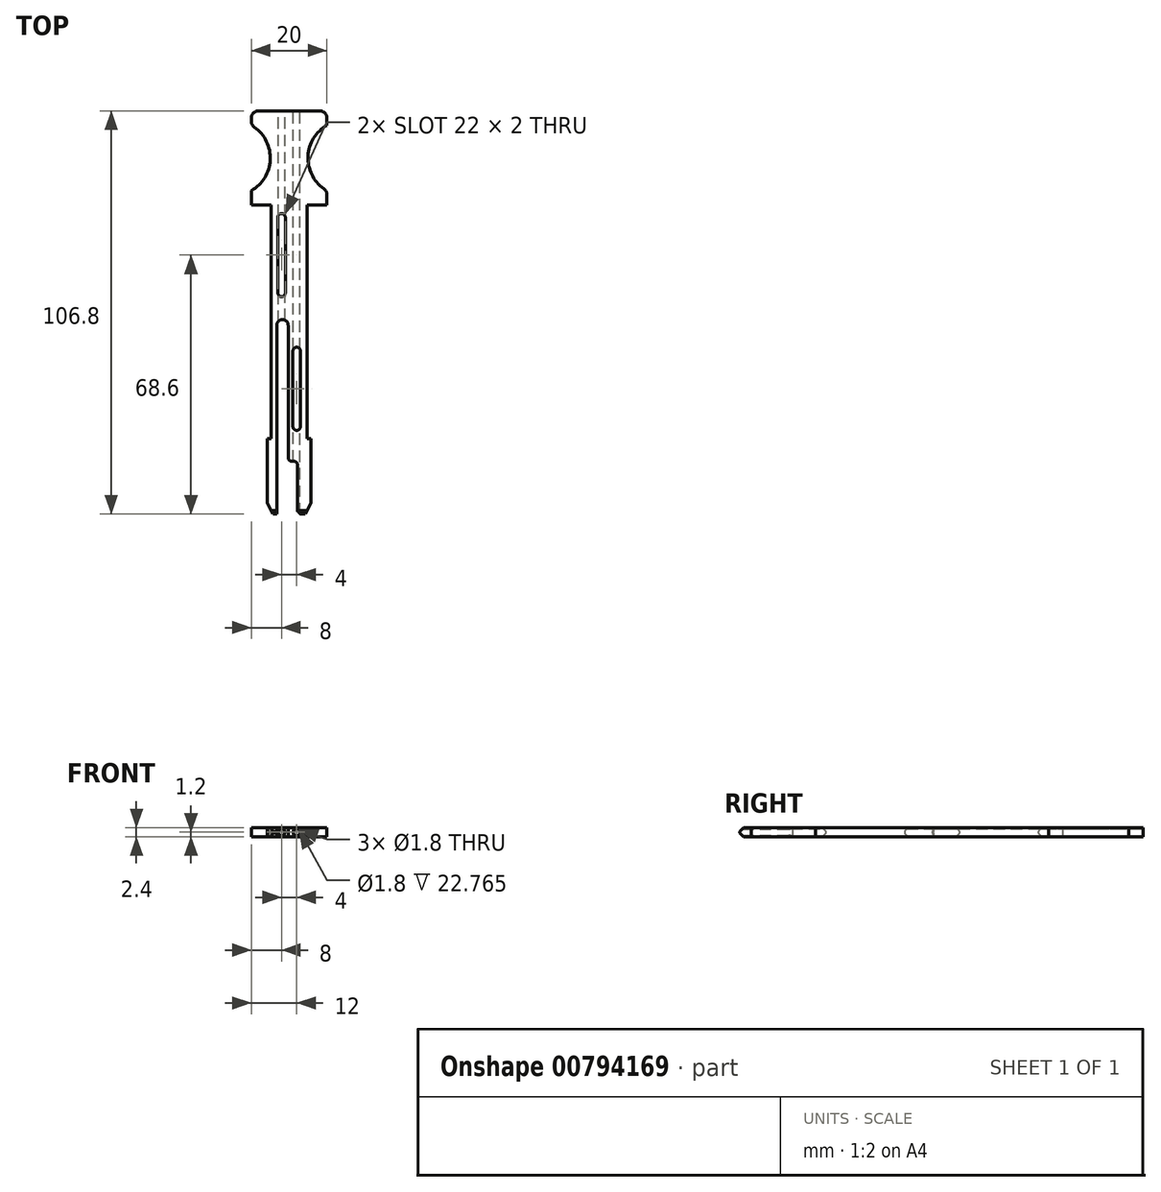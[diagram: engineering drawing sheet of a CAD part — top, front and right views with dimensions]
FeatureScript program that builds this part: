
annotation { "Feature Type Name" : "Feature", "Feature Type Description" : "" }
export const myFeature = defineFeature(function(context is Context, id is Id, definition is map)
    precondition{}
    {
        {
            var Q0;
            Q0=qCreatedBy(makeId("Top.planeOp"),FACE);
            var sketch = newSketch(context, id + "F0", { "sketchPlane" : qUnion([Q0])});
            skLineSegment(sketch, "E0", {"start": v(0, 0) * mm, "end": v(0, 61.8) * mm, "construction": true});
            skLineSegment(sketch, "E1.bottom", {"start": v(-10, 61.8) * mm, "end": v(-4.75, 61.8) * mm});
            skLineSegment(sketch, "E1.top", {"start": v(-5.75, 0) * mm, "end": v(-4.75, 0) * mm});
            skLineSegment(sketch, "E1.left", {"start": v(-4.75, 61.8) * mm, "end": v(-4.75, 0) * mm});
            skLineSegment(sketch, "E1.right", {"start": v(4.75, 61.8) * mm, "end": v(4.75, 0) * mm});
            skLineSegment(sketch, "E2", {"start": v(-5.75, 0) * mm, "end": v(-5.75, -20) * mm});
            skLineSegment(sketch, "E3", {"start": v(-5.75, -20) * mm, "end": v(5.75, -20) * mm});
            skLineSegment(sketch, "E4", {"start": v(5.75, -20) * mm, "end": v(5.75, 0) * mm});
            skLineSegment(sketch, "E5.trimOffspring", {"start": v(4.75, 0) * mm, "end": v(5.75, 0) * mm});
            skLineSegment(sketch, "E6", {"start": v(-10, 61.8) * mm, "end": v(-10, 86.8) * mm});
            skLineSegment(sketch, "E7", {"start": v(-10, 86.8) * mm, "end": v(10, 86.8) * mm});
            skLineSegment(sketch, "E8", {"start": v(10, 86.8) * mm, "end": v(10, 61.8) * mm});
            skLineSegment(sketch, "E9.trimOffspring", {"start": v(4.75, 61.8) * mm, "end": v(10, 61.8) * mm});
            skSolve(sketch);
        }
        {
            var Q0;
            Q0 = qSketchRegion(id + "F0", true);
            extrude(context, id + "F1", {"entities" : qUnion([Q0]), "depth" : 2.4 * mm, "offsetDistance" : 25 * mm});
        }
        {
            var Q0;
            Q0=qCreatedBy(makeId("Top.planeOp"),FACE);
            var sketch = newSketch(context, id + "F2", { "sketchPlane" : qUnion([Q0])});
            skLineSegment(sketch, "E10.0", {"start": v(-3.25, -20) * mm, "end": v(2.25, -20) * mm});
            skLineSegment(sketch, "E11", {"start": v(-3.25, -20) * mm, "end": v(-3.25, 30) * mm});
            skLineSegment(sketch, "E12", {"start": v(-0.25, 30) * mm, "end": v(-0.25, -5) * mm});
            skPoint(sketch, "E13.orphan", {"position": v(-5.75, -20) * mm});
            skPoint(sketch, "E14.orphan", {"position": v(5.75, -20) * mm});
            skArc(sketch, "E15", {"start": v(-0.25, 30) * mm, "mid": v(-1.75, 31.5) * mm, "end": v(-3.25, 30) * mm});
            skLineSegment(sketch, "E16", {"start": v(2.25, -20) * mm, "end": v(2.25, -7) * mm});
            skLineSegment(sketch, "E17", {"start": v(1.25, -6) * mm, "end": v(0.75, -6) * mm});
            skPoint(sketch, "E18.visualSharp", {"position": v(2.25, -6) * mm});
            skArc(sketch, "E18.filletArc", {"start": v(2.25, -7) * mm, "mid": v(1.96, -6.3) * mm, "end": v(1.25, -6) * mm});
            skPoint(sketch, "E19.visualSharp", {"position": v(-0.25, -6) * mm});
            skArc(sketch, "E19.filletArc", {"start": v(-0.25, -5) * mm, "mid": v(0.04, -5.7) * mm, "end": v(0.75, -6) * mm});
            skSolve(sketch);
        }
        {
            var Q0;
            Q0 = qSketchRegion(id + "F2", true);
            var Q1;
            Q1 = qConstructionFilter(qBodyType(qCreatedBy(id + "F2" ,EDGE), BodyType.WIRE), ConstructionObject.NO);
            extrude(context, id + "F3", {"entities" : qUnion([Q0]), "operationType" : NewBodyOperationType.REMOVE, "surfaceEntities" : qUnion([Q1]), "endBound" : BoundingType.THROUGH_ALL, "depth" : 25 * mm, "offsetDistance" : 25 * mm});
        }
        {
            var Q0;
            Q0=makeQuery(id+"F1.opExtrude","SWEPT_FACE",FACE,{"disambiguationData":[OSD([sQuery(id+"F0.wireOp",EDGE,"E7")])]});
            var sketch = newSketch(context, id + "F4", { "sketchPlane" : qUnion([Q0])});
            skCircle(sketch, "E20", {"center": v(-2, 1.2) * mm, "radius": 0.9 * mm});
            skCircle(sketch, "E21", {"center": v(2, 1.2) * mm, "radius": 0.9 * mm});
            skSolve(sketch);
        }
        {
            var Q0;
            Q0 = qSketchRegion(id + "F4", true);
            extrude(context, id + "F5", {"entities" : qUnion([Q0]), "operationType" : NewBodyOperationType.REMOVE, "endBound" : BoundingType.THROUGH_ALL, "oppositeDirection" : true, "depth" : 25 * mm, "offsetDistance" : 25 * mm});
        }
        {
            var Q0;
            Q0=makeQuery(id+"F1.opExtrude","CAP_FACE",FACE,{"disambiguationData":[OSD([sQuery(id+"F0.wireOp",EDGE,"E1.bottom"),sQuery(id+"F0.wireOp",EDGE,"E1.top"),sQuery(id+"F0.wireOp",EDGE,"E1.left"),sQuery(id+"F0.wireOp",EDGE,"E1.right"),sQuery(id+"F0.wireOp",EDGE,"E2"),sQuery(id+"F0.wireOp",EDGE,"E3"),sQuery(id+"F0.wireOp",EDGE,"E4"),sQuery(id+"F0.wireOp",EDGE,"E5.trimOffspring"),sQuery(id+"F0.wireOp",EDGE,"E6"),sQuery(id+"F0.wireOp",EDGE,"E7"),sQuery(id+"F0.wireOp",EDGE,"E8"),sQuery(id+"F0.wireOp",EDGE,"E9.trimOffspring")])],"isStart":false});
            var sketch = newSketch(context, id + "F6", { "sketchPlane" : qUnion([Q0])});
            skLineSegment(sketch, "E22", {"start": v(4.75, 13.2) * mm, "end": v(-4.75, 13.2) * mm, "construction": true});
            skLineSegment(sketch, "E23.left", {"start": v(1, 3.2) * mm, "end": v(1, 23.2) * mm});
            skLineSegment(sketch, "E23.right", {"start": v(3, 3.2) * mm, "end": v(3, 23.2) * mm});
            skPoint(sketch, "E23.middle", {"position": v(2, 13.2) * mm});
            skArc(sketch, "E24", {"start": v(3, 3.2) * mm, "mid": v(2, 2.2) * mm, "end": v(1, 3.2) * mm});
            skArc(sketch, "E25", {"start": v(1, 23.2) * mm, "mid": v(2, 24.2) * mm, "end": v(3, 23.2) * mm});
            skSolve(sketch);
        }
        {
            var Q0;
            Q0 = qSketchRegion(id + "F6", true);
            extrude(context, id + "F7", {"entities" : qUnion([Q0]), "operationType" : NewBodyOperationType.REMOVE, "endBound" : BoundingType.THROUGH_ALL, "oppositeDirection" : true, "depth" : 25 * mm, "offsetDistance" : 25 * mm});
        }
        {
            var Q0;
            Q0=makeQuery(id+"F1.opExtrude","CAP_FACE",FACE,{"disambiguationData":[OSD([sQuery(id+"F0.wireOp",EDGE,"E1.bottom"),sQuery(id+"F0.wireOp",EDGE,"E1.top"),sQuery(id+"F0.wireOp",EDGE,"E1.left"),sQuery(id+"F0.wireOp",EDGE,"E1.right"),sQuery(id+"F0.wireOp",EDGE,"E2"),sQuery(id+"F0.wireOp",EDGE,"E3"),sQuery(id+"F0.wireOp",EDGE,"E4"),sQuery(id+"F0.wireOp",EDGE,"E5.trimOffspring"),sQuery(id+"F0.wireOp",EDGE,"E6"),sQuery(id+"F0.wireOp",EDGE,"E7"),sQuery(id+"F0.wireOp",EDGE,"E8"),sQuery(id+"F0.wireOp",EDGE,"E9.trimOffspring")])],"isStart":false});
            var sketch = newSketch(context, id + "F8", { "sketchPlane" : qUnion([Q0])});
            skLineSegment(sketch, "E26", {"start": v(4.75, 48.6) * mm, "end": v(-4.75, 48.6) * mm, "construction": true});
            skLineSegment(sketch, "E27.left", {"start": v(-3, 58.6) * mm, "end": v(-3, 38.6) * mm});
            skLineSegment(sketch, "E27.right", {"start": v(-1, 58.6) * mm, "end": v(-1, 38.6) * mm});
            skPoint(sketch, "E27.middle", {"position": v(-2, 48.6) * mm});
            skArc(sketch, "E28", {"start": v(-1, 38.6) * mm, "mid": v(-2, 37.6) * mm, "end": v(-3, 38.6) * mm});
            skArc(sketch, "E29", {"start": v(-3, 58.6) * mm, "mid": v(-2, 59.6) * mm, "end": v(-1, 58.6) * mm});
            skSolve(sketch);
        }
        {
            var Q0;
            Q0 = qSketchRegion(id + "F8", true);
            extrude(context, id + "F9", {"entities" : qUnion([Q0]), "operationType" : NewBodyOperationType.REMOVE, "endBound" : BoundingType.THROUGH_ALL, "oppositeDirection" : true, "depth" : 25 * mm, "offsetDistance" : 25 * mm});
        }
        {
            var Q0;
            Q0=makeQuery(id+"F1.opExtrude","SWEPT_EDGE",EDGE,{"disambiguationData":[OSD([sQuery(id+"F0.wireOp",EDGE,"E3"),sQuery(id+"F0.wireOp",EDGE,"E4")])]});
            chamfer(context, id + "F10", {"entities" : qUnion([Q0]), "chamferType" : ChamferType.TWO_OFFSETS, "width1" : 3 * mm, "oppositeDirection" : false, "width2" : 1.5 * mm, "tangentPropagation" : true});
        }
        {
            var Q0;
            Q0=makeQuery(id+"F1.opExtrude","SWEPT_EDGE",EDGE,{"disambiguationData":[OSD([sQuery(id+"F0.wireOp",EDGE,"E2"),sQuery(id+"F0.wireOp",EDGE,"E3")])]});
            chamfer(context, id + "F11", {"entities" : qUnion([Q0]), "chamferType" : ChamferType.TWO_OFFSETS, "width1" : 1.5 * mm, "oppositeDirection" : false, "width2" : 3 * mm, "tangentPropagation" : true});
        }
        {
            var Q0;
            {var subQ0=sQuery(id+"F0.wireOp",EDGE,"E3");var subQ1=sQuery(id+"F0.wireOp",EDGE,"E2");Q0=makeQuery(id+"F3.boolean.opBoolean","SPLIT",EDGE,{"disambiguationData":[TD([makeQuery(id+"F1.opExtrude","SWEPT_FACE",FACE,{"disambiguationData":[OSD([subQ1])]})])],"derivedFrom":makeQuery(id+"F1.opExtrude","CAP_EDGE",EDGE,{"disambiguationData":[OSD([subQ0])],"isStart":false})});}
            var Q1;
            {var subQ0=sQuery(id+"F0.wireOp",EDGE,"E3");var subQ1=sQuery(id+"F0.wireOp",EDGE,"E2");Q1=makeQuery(id+"F3.boolean.opBoolean","SPLIT",EDGE,{"disambiguationData":[TD([makeQuery(id+"F1.opExtrude","SWEPT_FACE",FACE,{"disambiguationData":[OSD([subQ1])]})])],"derivedFrom":makeQuery(id+"F1.opExtrude","CAP_EDGE",EDGE,{"disambiguationData":[OSD([subQ0])],"isStart":true})});}
            var Q2;
            {var subQ0=sQuery(id+"F0.wireOp",EDGE,"E4");var subQ1=sQuery(id+"F0.wireOp",EDGE,"E3");Q2=makeQuery(id+"F3.boolean.opBoolean","SPLIT",EDGE,{"disambiguationData":[TD([makeQuery(id+"F1.opExtrude","SWEPT_FACE",FACE,{"disambiguationData":[OSD([subQ0])]})])],"derivedFrom":makeQuery(id+"F1.opExtrude","CAP_EDGE",EDGE,{"disambiguationData":[OSD([subQ1])],"isStart":false})});}
            var Q3;
            {var subQ0=sQuery(id+"F0.wireOp",EDGE,"E4");var subQ1=sQuery(id+"F0.wireOp",EDGE,"E3");Q3=makeQuery(id+"F3.boolean.opBoolean","SPLIT",EDGE,{"disambiguationData":[TD([makeQuery(id+"F1.opExtrude","SWEPT_FACE",FACE,{"disambiguationData":[OSD([subQ0])]})])],"derivedFrom":makeQuery(id+"F1.opExtrude","CAP_EDGE",EDGE,{"disambiguationData":[OSD([subQ1])],"isStart":true})});}
            chamfer(context, id + "F12", {"entities" : qUnion([Q0, Q1, Q2, Q3]), "width" : 1 * mm, "tangentPropagation" : true});
        }
        {
            var Q0;
            Q0=makeQuery(id+"F1.opExtrude","CAP_FACE",FACE,{"disambiguationData":[OSD([sQuery(id+"F0.wireOp",EDGE,"E1.bottom"),sQuery(id+"F0.wireOp",EDGE,"E1.top"),sQuery(id+"F0.wireOp",EDGE,"E1.left"),sQuery(id+"F0.wireOp",EDGE,"E1.right"),sQuery(id+"F0.wireOp",EDGE,"E2"),sQuery(id+"F0.wireOp",EDGE,"E3"),sQuery(id+"F0.wireOp",EDGE,"E4"),sQuery(id+"F0.wireOp",EDGE,"E5.trimOffspring"),sQuery(id+"F0.wireOp",EDGE,"E6"),sQuery(id+"F0.wireOp",EDGE,"E7"),sQuery(id+"F0.wireOp",EDGE,"E8"),sQuery(id+"F0.wireOp",EDGE,"E9.trimOffspring")])],"isStart":false});
            var sketch = newSketch(context, id + "F13", { "sketchPlane" : qUnion([Q0])});
            skLineSegment(sketch, "E30.0", {"start": v(10, 82.96) * mm, "end": v(10, 65.64) * mm});
            skLineSegment(sketch, "E31.0", {"start": v(-10, 65.64) * mm, "end": v(-10, 82.96) * mm});
            skArc(sketch, "E32", {"start": v(10, 82.96) * mm, "mid": v(5, 74.3) * mm, "end": v(10, 65.64) * mm});
            skArc(sketch, "E33", {"start": v(-10, 65.64) * mm, "mid": v(-5, 74.3) * mm, "end": v(-10, 82.96) * mm});
            skLineSegment(sketch, "E34", {"start": v(15, 74.3) * mm, "end": v(-15, 74.3) * mm, "construction": true});
            skPoint(sketch, "E35.orphan", {"position": v(-10, 61.8) * mm});
            skPoint(sketch, "E36.orphan", {"position": v(-10, 86.8) * mm});
            skPoint(sketch, "E37.orphan", {"position": v(10, 86.8) * mm});
            skPoint(sketch, "E38.orphan", {"position": v(10, 61.8) * mm});
            skSolve(sketch);
        }
        {
            var Q0;
            Q0 = qSketchRegion(id + "F13", true);
            extrude(context, id + "F14", {"entities" : qUnion([Q0]), "operationType" : NewBodyOperationType.REMOVE, "endBound" : BoundingType.THROUGH_ALL, "oppositeDirection" : true, "depth" : 25 * mm, "offsetDistance" : 25 * mm});
        }
        {
            var Q0;
            {var subQ0=sQuery(id+"F13.wireOp",EDGE,"E32");var subQ1=sQuery(id+"F13.wireOp",EDGE,"E30.0");var subQ2=sQuery(id+"F0.wireOp",EDGE,"E8");Q0=makeQuery(id+"F14.boolean.opBoolean","COPY",EDGE,{"derivedFrom":makeQuery(id+"F14.opExtrude","SWEPT_EDGE",EDGE,{"disambiguationData":[OSD([subQ2,subQ1,subQ0]),TDD([makeQuery(id+"F13.imprint","INTERSECT",VERTEX,{"disambiguationData":[OD(1.0)],"derivedFrom":[makeQuery(id+"F1.opExtrude","CAP_EDGE",EDGE,{"disambiguationData":[OSD([subQ2])],"isStart":false}),subQ1,subQ0]})])]})});}
            var Q1;
            {var subQ0=sQuery(id+"F13.wireOp",EDGE,"E32");var subQ1=sQuery(id+"F13.wireOp",EDGE,"E30.0");var subQ2=sQuery(id+"F0.wireOp",EDGE,"E8");Q1=makeQuery(id+"F14.boolean.opBoolean","COPY",EDGE,{"derivedFrom":makeQuery(id+"F14.opExtrude","SWEPT_EDGE",EDGE,{"disambiguationData":[OSD([subQ2,subQ1,subQ0]),TDD([makeQuery(id+"F13.imprint","INTERSECT",VERTEX,{"disambiguationData":[OD(0.0)],"derivedFrom":[makeQuery(id+"F1.opExtrude","CAP_EDGE",EDGE,{"disambiguationData":[OSD([subQ2])],"isStart":false}),subQ1,subQ0]})])]})});}
            var Q2;
            Q2=makeQuery(id+"F1.opExtrude","SWEPT_EDGE",EDGE,{"disambiguationData":[OSD([sQuery(id+"F0.wireOp",EDGE,"E7"),sQuery(id+"F0.wireOp",EDGE,"E8")])]});
            var Q3;
            {var subQ0=sQuery(id+"F13.wireOp",EDGE,"E33");var subQ1=sQuery(id+"F13.wireOp",EDGE,"E31.0");var subQ2=sQuery(id+"F0.wireOp",EDGE,"E6");Q3=makeQuery(id+"F14.boolean.opBoolean","COPY",EDGE,{"derivedFrom":makeQuery(id+"F14.opExtrude","SWEPT_EDGE",EDGE,{"disambiguationData":[OSD([subQ2,subQ1,subQ0]),TDD([makeQuery(id+"F13.imprint","INTERSECT",VERTEX,{"disambiguationData":[OD(0.0)],"derivedFrom":[makeQuery(id+"F1.opExtrude","CAP_EDGE",EDGE,{"disambiguationData":[OSD([subQ2])],"isStart":false}),subQ1,subQ0]})])]})});}
            var Q4;
            {var subQ0=sQuery(id+"F13.wireOp",EDGE,"E33");var subQ1=sQuery(id+"F13.wireOp",EDGE,"E31.0");var subQ2=sQuery(id+"F0.wireOp",EDGE,"E6");Q4=makeQuery(id+"F14.boolean.opBoolean","COPY",EDGE,{"derivedFrom":makeQuery(id+"F14.opExtrude","SWEPT_EDGE",EDGE,{"disambiguationData":[OSD([subQ2,subQ1,subQ0]),TDD([makeQuery(id+"F13.imprint","INTERSECT",VERTEX,{"disambiguationData":[OD(1.0)],"derivedFrom":[makeQuery(id+"F1.opExtrude","CAP_EDGE",EDGE,{"disambiguationData":[OSD([subQ2])],"isStart":false}),subQ1,subQ0]})])]})});}
            var Q5;
            Q5=makeQuery(id+"F1.opExtrude","SWEPT_EDGE",EDGE,{"disambiguationData":[OSD([sQuery(id+"F0.wireOp",EDGE,"E6"),sQuery(id+"F0.wireOp",EDGE,"E7")])]});
            fillet(context, id + "F15", {"entities" : qUnion([Q0, Q1, Q2, Q3, Q4, Q5]), "radius" : 2 * mm, "tangentPropagation" : true, "allowEdgeOverflow" : false});
        }
    });
